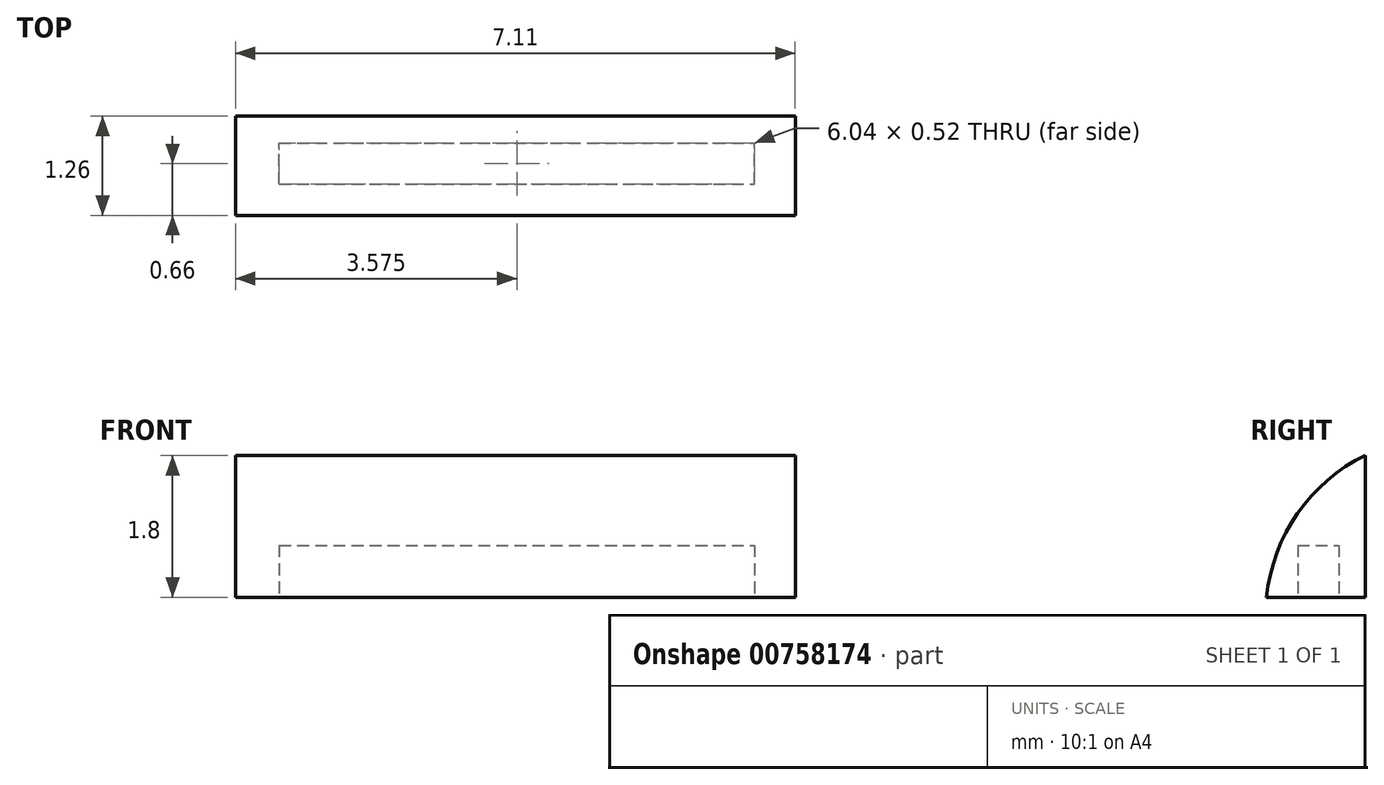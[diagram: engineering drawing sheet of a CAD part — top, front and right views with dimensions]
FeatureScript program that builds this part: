
annotation { "Feature Type Name" : "Feature", "Feature Type Description" : "" }
export const myFeature = defineFeature(function(context is Context, id is Id, definition is map)
    precondition{}
    {
        {
            var Q0;
            Q0=qCreatedBy(makeId("Front.planeOp"),FACE);
            var sketch = newSketch(context, id + "F0", { "sketchPlane" : qUnion([Q0])});
            skLineSegment(sketch, "E0.bottom", {"start": v(-57.8, 40.14) * mm, "end": v(-50.7, 40.14) * mm});
            skLineSegment(sketch, "E0.top", {"start": v(-57.8, 38.34) * mm, "end": v(-50.7, 38.34) * mm});
            skLineSegment(sketch, "E0.left", {"start": v(-57.8, 40.14) * mm, "end": v(-57.8, 38.34) * mm});
            skLineSegment(sketch, "E0.right", {"start": v(-50.7, 40.14) * mm, "end": v(-50.7, 38.34) * mm});
            skSolve(sketch);
        }
        {
            var Q0;
            Q0=makeQuery(id+"F0.imprint","IMPRINT",FACE,{"disambiguationData":[TD([[makeQuery(id+"F0.imprint","IMPRINT",EDGE,{"derivedFrom":sQuery(id+"F0.wireOp",EDGE,"E0.bottom")}),-1.0]])]});
            extrude(context, id + "F1", {"entities" : qUnion([Q0]), "depth" : 1.27 * mm, "offsetDistance" : 25.4 * mm});
        }
        {
            var Q0;
            Q0=makeQuery(id+"F1.opExtrude","SWEPT_FACE",FACE,{"disambiguationData":[OSD([sQuery(id+"F0.wireOp",EDGE,"E0.top")])]});
            var sketch = newSketch(context, id + "F2", { "sketchPlane" : qUnion([Q0])});
            skLineSegment(sketch, "E1.bottom", {"start": v(-57.25, 0.86) * mm, "end": v(-51.22, 0.86) * mm});
            skLineSegment(sketch, "E1.top", {"start": v(-57.25, 0.34) * mm, "end": v(-51.22, 0.34) * mm});
            skLineSegment(sketch, "E1.left", {"start": v(-57.25, 0.86) * mm, "end": v(-57.25, 0.34) * mm});
            skLineSegment(sketch, "E1.right", {"start": v(-51.22, 0.86) * mm, "end": v(-51.22, 0.34) * mm});
            skSolve(sketch);
        }
        {
            var Q0;
            Q0=makeQuery(id+"F2.imprint","IMPRINT",FACE,{"disambiguationData":[TD([[makeQuery(id+"F2.imprint","IMPRINT",EDGE,{"derivedFrom":sQuery(id+"F2.wireOp",EDGE,"E1.bottom")}),-1.0]])]});
            extrude(context, id + "F3", {"entities" : qUnion([Q0]), "operationType" : NewBodyOperationType.REMOVE, "oppositeDirection" : true, "depth" : 0.66 * mm, "offsetDistance" : 25.4 * mm});
        }
        {
            var Q0;
            Q0=makeQuery(id+"F1.opExtrude","CAP_EDGE",EDGE,{"disambiguationData":[OSD([sQuery(id+"F0.wireOp",EDGE,"E0.bottom")])],"isStart":false});
            fillet(context, id + "F4", {"entities" : qUnion([Q0]), "radius" : 2.27 * mm, "tangentPropagation" : true, "allowEdgeOverflow" : false});
        }
    });
